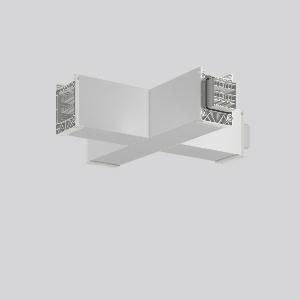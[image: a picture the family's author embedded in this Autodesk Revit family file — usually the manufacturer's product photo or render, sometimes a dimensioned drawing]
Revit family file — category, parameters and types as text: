
# Revit family: linedo_x-verbindung_982775_000_5c55
name_source: partatom
category: Lighting Fixtures
units: mm (PartAtom-declared; Revit-internal decimal feet)

## family parameters
Cut with Voids When Loaded = No
Host = Face
Light Source = No
Part Type = Normal
Room Calculation Point = No
Round Connector Dimension = Use Diameter
Shared = No

## types (1)
- LINEDO X-Verbindung
    Apparent Load = 0 VA
    Default Elevation = 1800 mm
    Description = Series: LINEDO
X-connector, 14-pole, connection plug / socket / plug / socket. Housing: extruded aluminium profile, anodised. Cover made of plastic, surface like housing. LINEDO plug system, plastic, light grey. Easy connection for rigid or flexible wires. 6 membrane cable entries (2 x M20 and 4 x M25). Suitable for power supply in 7-pole version. Ready prewired. Colour-coded individual cables enable easy electromechanical separation.
Colour: anodised aluminium
Length: 330 mm
Width: 330 mm
Height: 76 mm
Weight: 1410 g
    Height = 76 mm
    Lamp = 0 x
    Length = 331 mm
    Luminous efficacy = 0 lm/W
    Manufacturer = RZB
    ModVariant = No
    Model = 982775.000
    Mounting Place = Ceiling
    Mounting Type = Surface mounted
    Number of Poles = 1
    OnlyDefault = Yes
    Power Factor = 1
    Product Name = LINEDO X-Verbindung
    Product group = Continuous line luminaire system Linedo IP 54
    ProductGroupID = 314
    Protection Class = Protection class I
    Protection Degree = Degree of protection
    RLX_Detail_Level = 1
    RLX_Emergency_Light_Flux = 0 lm
    RLX_Emergency_Type = 0
    RLX_Emergency_Type_DB = No
    RlxData = <blob elided: 20125 chars, md5=28a412b5>
    Standby Power = 0 W
    System Light Flux = 0 lm
    System Power = 0 W
    Type Comments = Product without accessories
    Type Image = 982775.000.jpg
    URL = http://relux.com
    VarID = ---
    Voltage = 0 V
    Weight = 0.00 kg
    Width = 331 mm

## geometry (parser evidence)
native form markers: Blend x4, Sweep x11
no freeform markers — native parametric forms only
